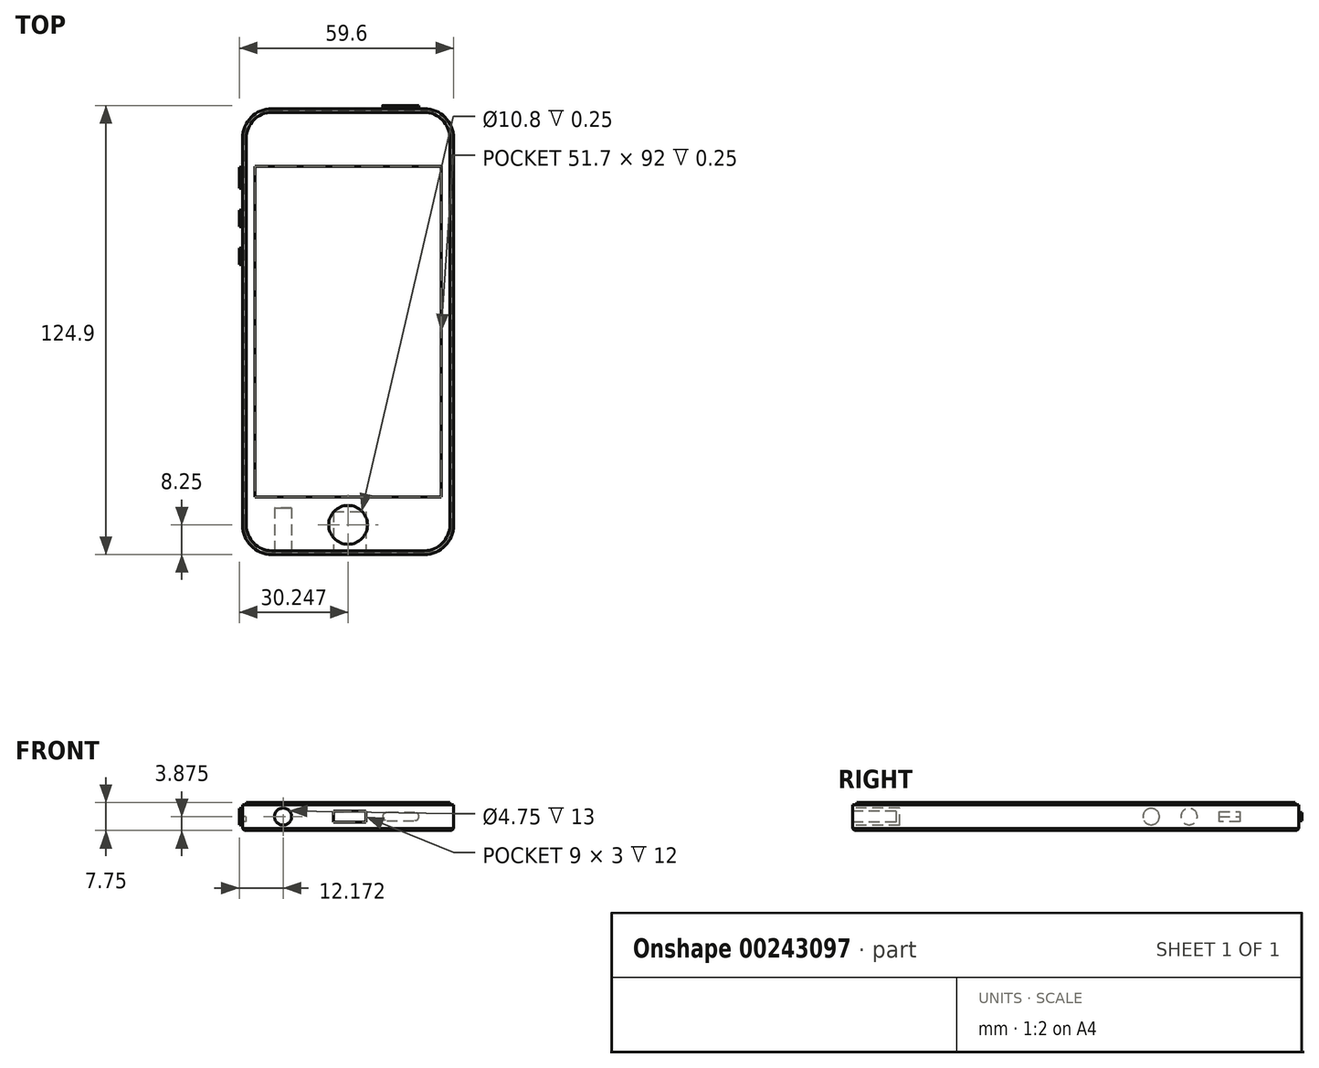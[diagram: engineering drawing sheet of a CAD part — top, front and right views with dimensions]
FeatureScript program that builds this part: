
annotation { "Feature Type Name" : "Feature", "Feature Type Description" : "" }
export const myFeature = defineFeature(function(context is Context, id is Id, definition is map)
    precondition{}
    {
        {
            var Q0;
            Q0=qCreatedBy(makeId("Top.planeOp"),FACE);
            var sketch = newSketch(context, id + "F0", { "sketchPlane" : qUnion([Q0])});
            skLineSegment(sketch, "E0.bottom", {"start": v(30.56, 124) * mm, "end": v(89.26, 124) * mm});
            skLineSegment(sketch, "E0.top", {"start": v(30.56, 0) * mm, "end": v(89.26, 0) * mm});
            skLineSegment(sketch, "E0.left", {"start": v(30.56, 124) * mm, "end": v(30.56, 0) * mm});
            skLineSegment(sketch, "E0.right", {"start": v(89.26, 124) * mm, "end": v(89.26, 0) * mm});
            skSolve(sketch);
        }
        {
            var Q0;
            Q0=makeQuery(id+"F0.imprint","IMPRINT",FACE,{"disambiguationData":[TD([[makeQuery(id+"F0.imprint","IMPRINT",EDGE,{"derivedFrom":sQuery(id+"F0.wireOp",EDGE,"E0.bottom")}),-1.0]])]});
            extrude(context, id + "F1", {"entities" : qUnion([Q0]), "depth" : 7.75 * mm});
        }
        {
            var Q0;
            Q0=makeQuery(id+"F1.opExtrude","CAP_FACE",FACE,{"disambiguationData":[OSD([sQuery(id+"F0.wireOp",EDGE,"E0.bottom"),sQuery(id+"F0.wireOp",EDGE,"E0.top"),sQuery(id+"F0.wireOp",EDGE,"E0.left"),sQuery(id+"F0.wireOp",EDGE,"E0.right")])],"isStart":false});
            var sketch = newSketch(context, id + "F2", { "sketchPlane" : qUnion([Q0])});
            skLineSegment(sketch, "E1", {"start": v(30.56, 0) * mm, "end": v(30.56, 16) * mm, "construction": true});
            skLineSegment(sketch, "E2", {"start": v(30.56, 124) * mm, "end": v(30.56, 108) * mm, "construction": true});
            skLineSegment(sketch, "E3", {"start": v(89.26, 124) * mm, "end": v(80.16, 124) * mm, "construction": true});
            skLineSegment(sketch, "E4", {"start": v(80.16, 124) * mm, "end": v(70.66, 124) * mm});
            skPoint(sketch, "E5", {"position": v(30.56, 113.5) * mm});
            skPoint(sketch, "E5.positionSnap0", {"position": v(30.56, 116) * mm});
            skLineSegment(sketch, "E6", {"start": v(89.26, 0) * mm, "end": v(89.26, 13.65) * mm, "construction": true});
            skCircle(sketch, "E7", {"center": v(59.9, 8.25) * mm, "radius": 5.4 * mm});
            skLineSegment(sketch, "E8", {"start": v(85.76, 16) * mm, "end": v(34.06, 16) * mm});
            skLineSegment(sketch, "E9", {"start": v(34.06, 16) * mm, "end": v(34.06, 108) * mm});
            skLineSegment(sketch, "E10", {"start": v(34.06, 108) * mm, "end": v(85.76, 108) * mm});
            skLineSegment(sketch, "E11", {"start": v(85.76, 108) * mm, "end": v(85.76, 16) * mm});
            skSolve(sketch);
        }
        {
            var Q0;
            Q0=makeQuery(id+"F1.opExtrude","SWEPT_FACE",FACE,{"disambiguationData":[OSD([sQuery(id+"F0.wireOp",EDGE,"E0.left")])]});
            var sketch = newSketch(context, id + "F3", { "sketchPlane" : qUnion([Q0])});
            skLineSegment(sketch, "E12", {"start": v(-124, 7.75) * mm, "end": v(-107.5, 7.75) * mm, "construction": true});
            skLineSegment(sketch, "E13", {"start": v(-107.5, 7.75) * mm, "end": v(-91.25, 7.75) * mm, "construction": true});
            skLineSegment(sketch, "E14", {"start": v(-91.25, 7.75) * mm, "end": v(-91.25, 0) * mm});
            skLineSegment(sketch, "E15", {"start": v(-91.25, 3.88) * mm, "end": v(-93.52, 3.88) * mm});
            skCircle(sketch, "E16", {"center": v(-93.52, 3.88) * mm, "radius": 2.27 * mm});
            skLineSegment(sketch, "E17", {"start": v(-91.25, 3.88) * mm, "end": v(-85.25, 3.88) * mm});
            skLineSegment(sketch, "E18", {"start": v(-85.25, 3.88) * mm, "end": v(-82.97, 3.88) * mm});
            skCircle(sketch, "E19", {"center": v(-82.97, 3.88) * mm, "radius": 2.27 * mm});
            skLineSegment(sketch, "E20", {"start": v(-93.52, 3.88) * mm, "end": v(-95.8, 3.88) * mm, "construction": true});
            skPoint(sketch, "E21.0", {"position": v(-124, 7.75) * mm});
            skLineSegment(sketch, "E22", {"start": v(-124, 7.75) * mm, "end": v(-101.9, 7.75) * mm, "construction": true});
            skLineSegment(sketch, "E23", {"start": v(-124, 0) * mm, "end": v(-107.7, 0) * mm, "construction": true});
            skLineSegment(sketch, "E24", {"start": v(-107.7, 3.88) * mm, "end": v(-107.7, 2.52) * mm});
            skLineSegment(sketch, "E25", {"start": v(-107.7, 2.52) * mm, "end": v(-101.9, 2.52) * mm});
            skLineSegment(sketch, "E26", {"start": v(-101.9, 2.52) * mm, "end": v(-101.9, 3.88) * mm});
            skLineSegment(sketch, "E27", {"start": v(-101.9, 3.88) * mm, "end": v(-101.9, 5.22) * mm});
            skLineSegment(sketch, "E28", {"start": v(-101.9, 5.22) * mm, "end": v(-107.7, 5.22) * mm});
            skLineSegment(sketch, "E29", {"start": v(-107.7, 5.22) * mm, "end": v(-107.7, 3.88) * mm});
            skLineSegment(sketch, "E30", {"start": v(-101.9, 3.88) * mm, "end": v(-107.7, 3.88) * mm});
            skSolve(sketch);
        }
        {
            var Q0;
            Q0=makeQuery(id+"F1.opExtrude","SWEPT_FACE",FACE,{"disambiguationData":[OSD([sQuery(id+"F0.wireOp",EDGE,"E0.top")])]});
            var sketch = newSketch(context, id + "F4", { "sketchPlane" : qUnion([Q0])});
            skLineSegment(sketch, "E31", {"start": v(89.26, 7.75) * mm, "end": v(80.5, 7.75) * mm, "construction": true});
            skLineSegment(sketch, "E32", {"start": v(80.5, 7.75) * mm, "end": v(67.96, 7.75) * mm, "construction": true});
            skLineSegment(sketch, "E33", {"start": v(89.26, 3.88) * mm, "end": v(30.56, 3.88) * mm, "construction": true});
            skLineSegment(sketch, "E34", {"start": v(80.5, 3.88) * mm, "end": v(80.5, 5.45) * mm});
            skLineSegment(sketch, "E35", {"start": v(80.5, 3.88) * mm, "end": v(80.5, 2.3) * mm});
            skLineSegment(sketch, "E36", {"start": v(80.5, 5.45) * mm, "end": v(67.96, 5.45) * mm});
            skLineSegment(sketch, "E37", {"start": v(67.96, 5.45) * mm, "end": v(67.96, 2.3) * mm});
            skLineSegment(sketch, "E38", {"start": v(67.96, 2.3) * mm, "end": v(80.5, 2.3) * mm});
            skLineSegment(sketch, "E39", {"start": v(67.96, 7.75) * mm, "end": v(64.8, 7.75) * mm, "construction": true});
            skLineSegment(sketch, "E40", {"start": v(64.8, 7.75) * mm, "end": v(55.8, 7.75) * mm, "construction": true});
            skLineSegment(sketch, "E41", {"start": v(55.8, 7.75) * mm, "end": v(52.66, 7.75) * mm, "construction": true});
            skLineSegment(sketch, "E42", {"start": v(52.66, 7.75) * mm, "end": v(45.2, 7.75) * mm, "construction": true});
            skLineSegment(sketch, "E43", {"start": v(52.66, 3.88) * mm, "end": v(52.66, 2.3) * mm, "construction": true});
            skLineSegment(sketch, "E44", {"start": v(52.66, 2.3) * mm, "end": v(45.2, 2.3) * mm});
            skLineSegment(sketch, "E45", {"start": v(45.2, 2.3) * mm, "end": v(45.2, 5.45) * mm});
            skLineSegment(sketch, "E46", {"start": v(45.2, 5.45) * mm, "end": v(52.66, 5.45) * mm});
            skLineSegment(sketch, "E47", {"start": v(52.66, 5.45) * mm, "end": v(52.66, 2.3) * mm});
            skLineSegment(sketch, "E48", {"start": v(55.8, 5.39) * mm, "end": v(64.8, 5.39) * mm});
            skLineSegment(sketch, "E49", {"start": v(64.8, 5.39) * mm, "end": v(64.8, 2.39) * mm});
            skLineSegment(sketch, "E50", {"start": v(64.8, 2.39) * mm, "end": v(55.8, 2.39) * mm});
            skLineSegment(sketch, "E51", {"start": v(55.8, 5.39) * mm, "end": v(55.8, 2.39) * mm});
            skPoint(sketch, "E52.endSnap0", {"position": v(41.83, 5.45) * mm});
            skCircle(sketch, "E53", {"center": v(41.83, 3.88) * mm, "radius": 2.37 * mm});
            skSolve(sketch);
        }
        {
            var Q0;
            Q0=makeQuery(id+"F1.opExtrude","SWEPT_EDGE",EDGE,{"disambiguationData":[OSD([sQuery(id+"F0.wireOp",EDGE,"E0.bottom"),sQuery(id+"F0.wireOp",EDGE,"E0.left")])]});
            var Q1;
            Q1=makeQuery(id+"F1.opExtrude","SWEPT_EDGE",EDGE,{"disambiguationData":[OSD([sQuery(id+"F0.wireOp",EDGE,"E0.bottom"),sQuery(id+"F0.wireOp",EDGE,"E0.right")])]});
            var Q2;
            Q2=makeQuery(id+"F1.opExtrude","SWEPT_EDGE",EDGE,{"disambiguationData":[OSD([sQuery(id+"F0.wireOp",EDGE,"E0.top"),sQuery(id+"F0.wireOp",EDGE,"E0.left")])]});
            var Q3;
            Q3=makeQuery(id+"F1.opExtrude","SWEPT_EDGE",EDGE,{"disambiguationData":[OSD([sQuery(id+"F0.wireOp",EDGE,"E0.top"),sQuery(id+"F0.wireOp",EDGE,"E0.right")])]});
            fillet(context, id + "F5", {"entities" : qUnion([Q0, Q1, Q2, Q3]), "radius" : 8.15 * mm, "tangentPropagation" : true, "allowEdgeOverflow" : false});
        }
        {
            var Q0;
            Q0=makeQuery(id+"F1.opExtrude","SWEPT_FACE",FACE,{"disambiguationData":[OSD([sQuery(id+"F0.wireOp",EDGE,"E0.bottom")])]});
            var sketch = newSketch(context, id + "F6", { "sketchPlane" : qUnion([Q0])});
            skLineSegment(sketch, "E54", {"start": v(-70.66, 0) * mm, "end": v(-80.16, 0) * mm, "construction": true});
            skArc(sketch, "E55", {"start": v(-78.5, 4.97) * mm, "mid": v(-79.6, 3.88) * mm, "end": v(-78.5, 2.78) * mm});
            skLineSegment(sketch, "E56", {"start": v(-78.5, 4.97) * mm, "end": v(-70.66, 4.98) * mm});
            skLineSegment(sketch, "E57", {"start": v(-70.66, 2.78) * mm, "end": v(-78.5, 2.78) * mm});
            skPoint(sketch, "E58.endSnap0", {"position": v(-70.66, 3.88) * mm});
            skArc(sketch, "E59", {"start": v(-70.66, 2.78) * mm, "mid": v(-69.56, 3.88) * mm, "end": v(-70.66, 4.98) * mm});
            skSolve(sketch);
        }
        {
            var Q0;
            Q0=makeQuery(id+"F4.imprint","IMPRINT",FACE,{"disambiguationData":[TD([[makeQuery(id+"F4.imprint","IMPRINT",EDGE,{"derivedFrom":sQuery(id+"F4.wireOp",EDGE,"E53")}),1.0]])]});
            extrude(context, id + "F7", {"entities" : qUnion([Q0]), "operationType" : NewBodyOperationType.REMOVE, "oppositeDirection" : true, "depth" : 13 * mm});
        }
        {
            var Q0;
            Q0 = qSketchRegion(id + "F6", true);
            extrude(context, id + "F8", {"entities" : qUnion([Q0]), "operationType" : NewBodyOperationType.ADD, "depth" : .9 * mm});
        }
        {
            var Q0;
            Q0=makeQuery(id+"F3.imprint","IMPRINT",FACE,{"disambiguationData":[TD([[makeQuery(id+"F3.imprint","IMPRINT",EDGE,{"derivedFrom":sQuery(id+"F3.wireOp",EDGE,"E16")}),1.0]])]});
            var Q1;
            Q1=makeQuery(id+"F3.imprint","IMPRINT",FACE,{"disambiguationData":[TD([[makeQuery(id+"F3.imprint","IMPRINT",EDGE,{"derivedFrom":sQuery(id+"F3.wireOp",EDGE,"E19")}),1.0]])]});
            var Q2;
            Q2=makeQuery(id+"F3.imprint","IMPRINT",FACE,{"disambiguationData":[TD([[makeQuery(id+"F3.imprint","IMPRINT",EDGE,{"derivedFrom":sQuery(id+"F3.wireOp",EDGE,"E27")}),1.0]])]});
            extrude(context, id + "F9", {"entities" : qUnion([Q0, Q1, Q2]), "operationType" : NewBodyOperationType.ADD, "depth" : .9 * mm});
        }
        {
            var Q0;
            Q0=makeQuery(id+"F3.imprint","IMPRINT",FACE,{"disambiguationData":[TD([[makeQuery(id+"F3.imprint","IMPRINT",EDGE,{"derivedFrom":sQuery(id+"F3.wireOp",EDGE,"E24")}),1.0]])]});
            extrude(context, id + "F10", {"entities" : qUnion([Q0]), "operationType" : NewBodyOperationType.REMOVE, "oppositeDirection" : true, "depth" : .9 * mm});
        }
        {
            var Q0;
            Q0=makeQuery(id+"F4.imprint","IMPRINT",FACE,{"disambiguationData":[TD([[makeQuery(id+"F4.imprint","IMPRINT",EDGE,{"derivedFrom":sQuery(id+"F4.wireOp",EDGE,"E48")}),-1.0]])]});
            extrude(context, id + "F11", {"entities" : qUnion([Q0]), "operationType" : NewBodyOperationType.REMOVE, "oppositeDirection" : true, "depth" : 12 * mm});
        }
        {
            var Q0;
            Q0=makeQuery(id+"F2.imprint","IMPRINT",FACE,{"disambiguationData":[TD([[makeQuery(id+"F2.imprint","IMPRINT",EDGE,{"derivedFrom":sQuery(id+"F2.wireOp",EDGE,"E7")}),1.0]])]});
            var Q1;
            Q1=sQuery(id+"F2.wireOp",EDGE,"E7");
            extrude(context, id + "F12", {"entities" : qUnion([Q0]), "operationType" : NewBodyOperationType.REMOVE, "surfaceEntities" : qUnion([Q1]), "oppositeDirection" : true, "depth" : .25 * mm});
        }
        {
            var Q0;
            {var subQ2=sQuery(id+"F2.wireOp",EDGE,"E4");Q0=makeQuery(id+"F2.imprint","IMPRINT",FACE,{"disambiguationData":[TD([[makeQuery(id+"F2.imprint","IMPRINT",EDGE,{"derivedFrom":subQ2}),-1.0]])]});}
            var sketch = newSketch(context, id + "F13", { "sketchPlane" : qUnion([Q0])});
            skArc(sketch, "E60.0", {"start": v(81.1, 0) * mm, "mid": v(86.87, 2.39) * mm, "end": v(89.26, 8.15) * mm});
            skLineSegment(sketch, "E61.0", {"start": v(89.26, 115.85) * mm, "end": v(89.26, 8.15) * mm});
            skLineSegment(sketch, "E62.0", {"start": v(38.7, 0) * mm, "end": v(81.1, 0) * mm});
            skArc(sketch, "E63.0", {"start": v(30.56, 8.15) * mm, "mid": v(32.94, 2.39) * mm, "end": v(38.7, 0) * mm});
            skLineSegment(sketch, "E64.0", {"start": v(30.56, 115.85) * mm, "end": v(30.56, 8.15) * mm});
            skArc(sketch, "E65.0", {"start": v(38.7, 124) * mm, "mid": v(32.94, 121.61) * mm, "end": v(30.56, 115.85) * mm});
            skLineSegment(sketch, "E66.0", {"start": v(38.7, 124) * mm, "end": v(81.1, 124) * mm});
            skArc(sketch, "E67.0", {"start": v(89.26, 115.85) * mm, "mid": v(86.87, 121.61) * mm, "end": v(81.1, 124) * mm});
            skArc(sketch, "E68", {"start": v(88.2, 8.15) * mm, "mid": v(86.13, 3.13) * mm, "end": v(81.1, 1.05) * mm});
            skLineSegment(sketch, "E69", {"start": v(81.1, 1.05) * mm, "end": v(38.7, 1.05) * mm});
            skArc(sketch, "E70", {"start": v(31.6, 8.15) * mm, "mid": v(33.69, 3.13) * mm, "end": v(38.7, 1.05) * mm});
            skLineSegment(sketch, "E71", {"start": v(31.6, 8.15) * mm, "end": v(31.6, 115.85) * mm});
            skArc(sketch, "E72", {"start": v(31.6, 115.85) * mm, "mid": v(33.69, 120.87) * mm, "end": v(38.7, 122.95) * mm});
            skLineSegment(sketch, "E73", {"start": v(38.7, 122.95) * mm, "end": v(81.1, 122.95) * mm});
            skArc(sketch, "E74", {"start": v(81.1, 122.95) * mm, "mid": v(86.13, 120.87) * mm, "end": v(88.2, 115.85) * mm});
            skLineSegment(sketch, "E75", {"start": v(88.2, 115.85) * mm, "end": v(88.2, 8.15) * mm});
            skSolve(sketch);
        }
        {
            var Q0;
            Q0 = qSketchRegion(id + "F13", true);
            extrude(context, id + "F14", {"entities" : qUnion([Q0]), "operationType" : NewBodyOperationType.REMOVE, "oppositeDirection" : true, "depth" : .55 * mm});
        }
        {
            var Q0;
            Q0=makeQuery(id+"F14.boolean.opBoolean","COPY",EDGE,{"derivedFrom":makeQuery(id+"F14.opExtrude","CAP_EDGE",EDGE,{"disambiguationData":[OSD([sQuery(id+"F13.wireOp",EDGE,"E66.0")])],"isStart":false})});
            var Q1;
            Q1=makeQuery(id+"F14.boolean.opBoolean","COPY",EDGE,{"derivedFrom":makeQuery(id+"F14.opExtrude","CAP_EDGE",EDGE,{"disambiguationData":[OSD([sQuery(id+"F13.wireOp",EDGE,"E67.0")])],"isStart":false})});
            var Q2;
            Q2=makeQuery(id+"F14.boolean.opBoolean","COPY",EDGE,{"derivedFrom":makeQuery(id+"F14.opExtrude","CAP_EDGE",EDGE,{"disambiguationData":[OSD([sQuery(id+"F13.wireOp",EDGE,"E61.0")])],"isStart":false})});
            var Q3;
            Q3=makeQuery(id+"F14.boolean.opBoolean","COPY",EDGE,{"derivedFrom":makeQuery(id+"F14.opExtrude","CAP_EDGE",EDGE,{"disambiguationData":[OSD([sQuery(id+"F13.wireOp",EDGE,"E60.0")])],"isStart":false})});
            var Q4;
            Q4=makeQuery(id+"F14.boolean.opBoolean","COPY",EDGE,{"derivedFrom":makeQuery(id+"F14.opExtrude","CAP_EDGE",EDGE,{"disambiguationData":[OSD([sQuery(id+"F13.wireOp",EDGE,"E62.0")])],"isStart":false})});
            var Q5;
            Q5=makeQuery(id+"F14.boolean.opBoolean","COPY",EDGE,{"derivedFrom":makeQuery(id+"F14.opExtrude","CAP_EDGE",EDGE,{"disambiguationData":[OSD([sQuery(id+"F13.wireOp",EDGE,"E63.0")])],"isStart":false})});
            var Q6;
            Q6=makeQuery(id+"F14.boolean.opBoolean","COPY",EDGE,{"derivedFrom":makeQuery(id+"F14.opExtrude","CAP_EDGE",EDGE,{"disambiguationData":[OSD([sQuery(id+"F13.wireOp",EDGE,"E64.0")])],"isStart":false})});
            var Q7;
            Q7=makeQuery(id+"F14.boolean.opBoolean","COPY",EDGE,{"derivedFrom":makeQuery(id+"F14.opExtrude","CAP_EDGE",EDGE,{"disambiguationData":[OSD([sQuery(id+"F13.wireOp",EDGE,"E65.0")])],"isStart":false})});
            var Q8;
            Q8=makeQuery(id+"F1.opExtrude","CAP_EDGE",EDGE,{"disambiguationData":[OSD([sQuery(id+"F0.wireOp",EDGE,"E0.right")])],"isStart":true});
            chamfer(context, id + "F15", {"entities" : qUnion([Q0, Q1, Q2, Q3, Q4, Q5, Q6, Q7, Q8]), "width" : .5 * mm, "tangentPropagation" : true});
        }
        {
            var Q0;
            Q0=makeQuery(id+"F2.imprint","IMPRINT",FACE,{"disambiguationData":[TD([[makeQuery(id+"F2.imprint","IMPRINT",EDGE,{"derivedFrom":sQuery(id+"F2.wireOp",EDGE,"E8")}),-1.0]])]});
            extrude(context, id + "F16", {"entities" : qUnion([Q0]), "operationType" : NewBodyOperationType.REMOVE, "oppositeDirection" : true, "depth" : .25 * mm});
        }
        {
            var Q0;
            {var subQ2=sQuery(id+"F2.wireOp",EDGE,"E4");Q0=makeQuery(id+"F2.imprint","IMPRINT",FACE,{"disambiguationData":[TD([[makeQuery(id+"F2.imprint","IMPRINT",EDGE,{"derivedFrom":subQ2}),-1.0]])]});}
            var sketch = newSketch(context, id + "F17", { "sketchPlane" : qUnion([Q0])});
            skPoint(sketch, "E76.0", {"position": v(34.06, 108) * mm});
            skLineSegment(sketch, "E77.0", {"start": v(30.56, 124) * mm, "end": v(30.56, 107.7) * mm});
            skLineSegment(sketch, "E78.0", {"start": v(31.06, 115.85) * mm, "end": v(31.06, 8.15) * mm});
            skLineSegment(sketch, "E79.0", {"start": v(31.6, 8.15) * mm, "end": v(31.6, 115.85) * mm});
            skLineSegment(sketch, "E80", {"start": v(31.06, 108) * mm, "end": v(30.56, 108) * mm});
            skLineSegment(sketch, "E81", {"start": v(34.06, 108) * mm, "end": v(31.6, 108) * mm});
            skLineSegment(sketch, "E82", {"start": v(31.06, 108) * mm, "end": v(31.6, 108) * mm});
            skLineSegment(sketch, "E83", {"start": v(30.56, 108) * mm, "end": v(30.56, 124) * mm});
            skSolve(sketch);
        }
        {
            var Q0;
            Q0=makeQuery(id+"F1.opExtrude","SWEPT_FACE",FACE,{"disambiguationData":[OSD([sQuery(id+"F0.wireOp",EDGE,"E0.bottom")])]});
            cPlane(context, id + "F18", {"entities" : qUnion([Q0]), "cplaneType" : CPlaneType.OFFSET, "offset" : 16 * mm, "oppositeDirection" : true, "width" : 150 * mm, "height" : 150 * mm});
        }
    });
